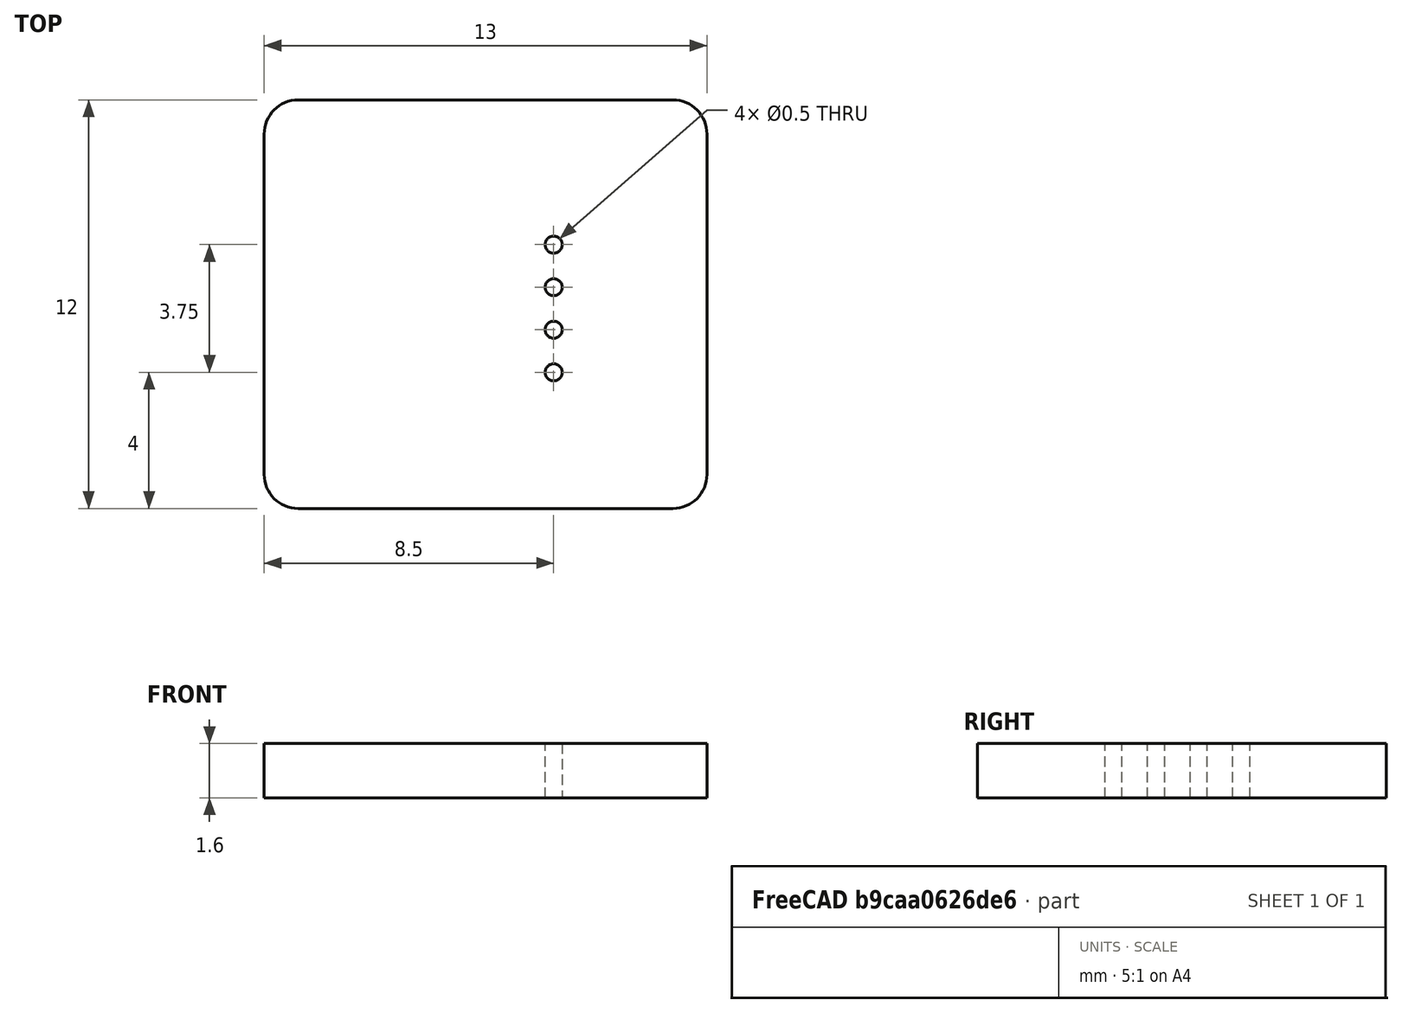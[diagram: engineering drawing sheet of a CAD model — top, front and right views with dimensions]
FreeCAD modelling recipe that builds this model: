
FCSTD DOCUMENT  (FreeCAD 0.16R6706 (Git))
Label: flex
License: All rights reserved
LicenseURL: http://en.wikipedia.org/wiki/All_rights_reserved
objects: App::DocumentObjectGroup×2, Part::Feature×1, Sketcher::SketchObject×1
note: 2 computed .brp shape members not serialized (recipe doc carries the construction recipe); baked Part::Feature solids carry a one-line shape summary decoded from their .brp

FEATURE [Part::Feature] Pcb
  Placement = pos=(-120.5,103,0) rot=(0,0,1;0rad)
  shape: bbox 13.01 x 12.01 x 1.61 mm, 14 faces (baked)
FEATURE [Sketcher::SketchObject] PCB_Sketch
  sketch-geometry (8):
    g0: LineSegment StartX=-6.5 StartY=5 StartZ=0 EndX=-6.5 EndY=-5 EndZ=0
    g1: LineSegment StartX=5.5 StartY=6 StartZ=0 EndX=-5.5 EndY=6 EndZ=0
    g2: LineSegment StartX=6.5 StartY=-5 StartZ=0 EndX=6.5 EndY=5 EndZ=0
    g3: LineSegment StartX=-5.5 StartY=-6 StartZ=0 EndX=5.5 EndY=-6 EndZ=0
    g4: ArcOfCircle CenterX=-5.5 CenterY=-5 CenterZ=0 NormalX=0 NormalY=0 NormalZ=1 Radius=1 StartAngle=3.14159 EndAngle=4.71239
    g5: ArcOfCircle CenterX=-5.5 CenterY=5 CenterZ=0 NormalX=0 NormalY=0 NormalZ=1 Radius=1 StartAngle=1.5708 EndAngle=3.14159
    g6: ArcOfCircle CenterX=5.5 CenterY=5 CenterZ=0 NormalX=0 NormalY=0 NormalZ=1 Radius=1 StartAngle=0 EndAngle=1.5708
    g7: ArcOfCircle CenterX=5.5 CenterY=-5 CenterZ=0 NormalX=0 NormalY=0 NormalZ=1 Radius=1 StartAngle=4.71239 EndAngle=6.28319
  constraints (12):
    c: Vertical(g0)
    c: Coincident(g0,g4)
    c: Coincident(g0,g5)
    c: Horizontal(g1)
    c: Coincident(g1,g5)
    c: Coincident(g1,g6)
    c: Vertical(g2)
    c: Coincident(g2,g6)
    c: Coincident(g2,g7)
    c: Horizontal(g3)
    c: Coincident(g3,g4)
    c: Coincident(g3,g7)
FEATURE [App::DocumentObjectGroup] Board_Geoms
  Group = -> [Pcb,PCB_Sketch]
FEATURE [App::DocumentObjectGroup] Step_Models
